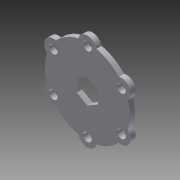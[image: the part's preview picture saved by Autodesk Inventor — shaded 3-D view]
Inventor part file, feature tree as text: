
AUTODESK INVENTOR PART (.ipt)
format: ipt  version: 2014 SP1 (Build 180222100, 222)  size: 142,848 bytes
history: native  units: in
note: dims shown in document units (in); Inventor stores cm internally (conversion verified against a paired STEP export)
features: extrude x3, sketch x2
ambient origin geometry x8: Origin, YZ Plane, XZ Plane, XY Plane, X Axis, Y Axis, Z Axis, Center Point
bodies: Solid1 (feature_tree)
feature tree (5):
  extrude  "Extrusion1"  Depth=0.204in
  sketch  "Sketch3"  dims[d8=0.125in d9=0.0in d10=2.3622in d12=360.0deg d14=0.438in d15=2.022in d16=2.3622in d18=360.0deg d20=0.125in d21=0.0in d22=0.125in d23=0.0in]
  extrude  "Extrusion3"  Depth=0.125in TaperAngle=360.0deg
  extrude  "Extrusion2"  Depth=0.125in
  sketch  "Sketch1"  dims[d6=1.875in d7=0.204in]
